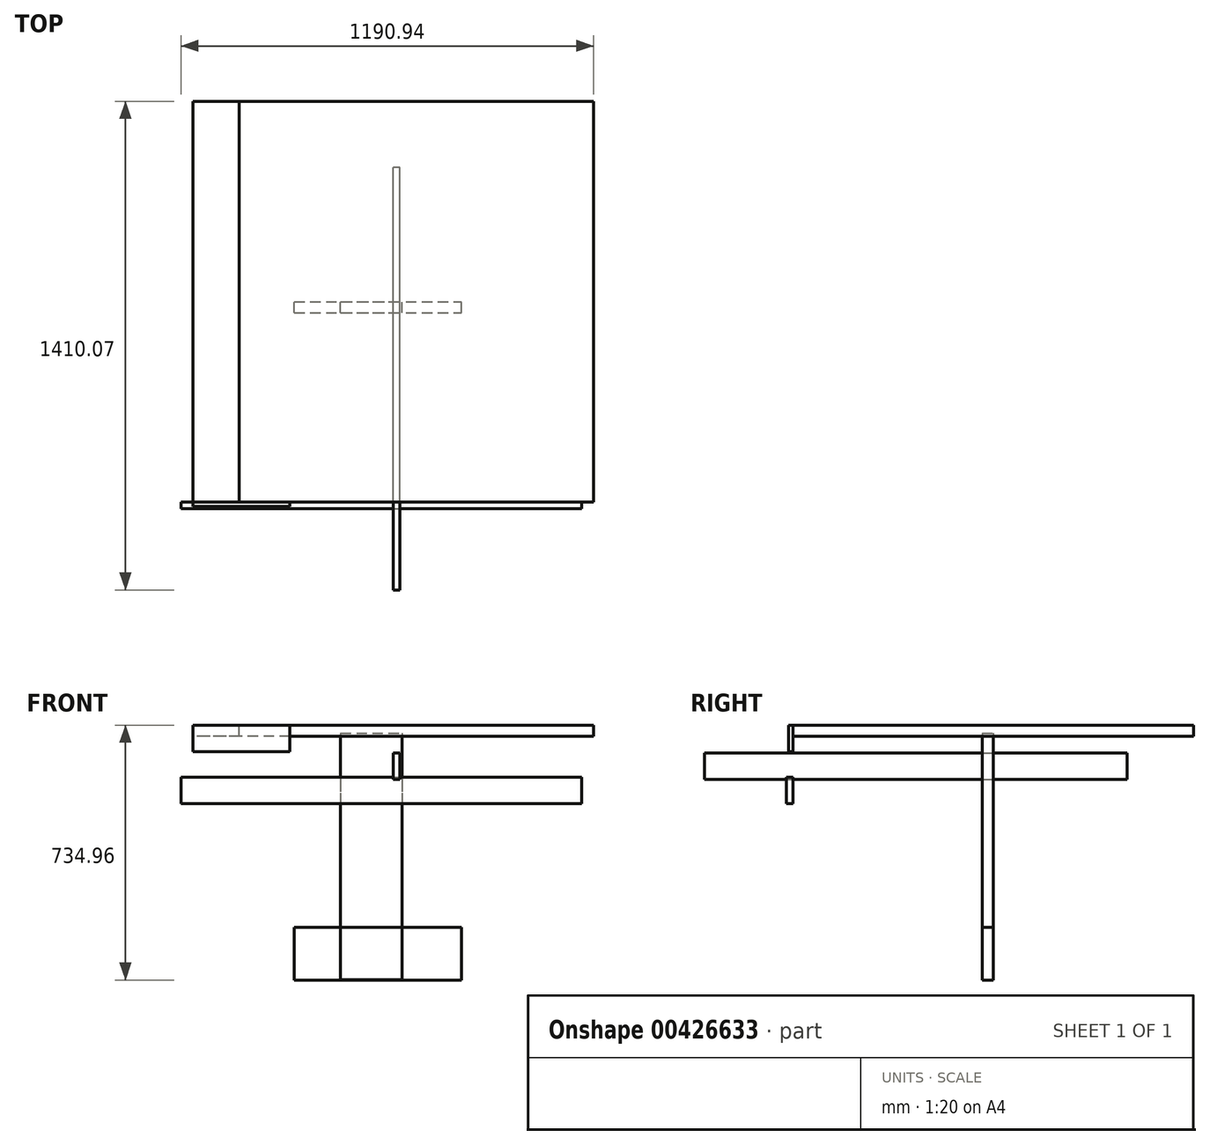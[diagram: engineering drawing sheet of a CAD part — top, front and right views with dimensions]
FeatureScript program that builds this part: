
annotation { "Feature Type Name" : "Feature", "Feature Type Description" : "" }
export const myFeature = defineFeature(function(context is Context, id is Id, definition is map)
    precondition{}
    {
        {
            var Q0;
            Q0=qCreatedBy(makeId("Top.planeOp"),FACE);
            var sketch = newSketch(context, id + "F0", { "sketchPlane" : qUnion([Q0])});
            skLineSegment(sketch, "E0.bottom", {"start": v(577.85, 577.85) * mm, "end": v(-577.85, 577.85) * mm});
            skLineSegment(sketch, "E0.top", {"start": v(577.85, -577.85) * mm, "end": v(-577.85, -577.85) * mm});
            skLineSegment(sketch, "E0.left", {"start": v(577.85, 577.85) * mm, "end": v(577.85, -577.85) * mm});
            skLineSegment(sketch, "E0.right", {"start": v(-577.85, 577.85) * mm, "end": v(-577.85, -577.85) * mm});
            skPoint(sketch, "E0.middle", {"position": v(0, 0) * mm});
            skLineSegment(sketch, "E1", {"start": v(0, 0) * mm, "end": v(0, 577.85) * mm, "construction": true});
            skLineSegment(sketch, "E2", {"start": v(0, 0) * mm, "end": v(0, -577.85) * mm, "construction": true});
            skLineSegment(sketch, "E3", {"start": v(0, -577.85) * mm, "end": v(0, 0) * mm, "construction": true});
            skLineSegment(sketch, "E4", {"start": v(0, 0) * mm, "end": v(577.85, 0) * mm, "construction": true});
            skLineSegment(sketch, "E5", {"start": v(577.85, 0) * mm, "end": v(-577.85, 0) * mm, "construction": true});
            skSolve(sketch);
        }
        {
            var Q0;
            Q0 = qSketchRegion(id + "F0", true);
            extrude(context, id + "F1", {"entities" : qUnion([Q0]), "depth" : 31.75 * mm});
        }
        {
            var Q0;
            Q0=makeQuery(id+"F1.opExtrude","SWEPT_FACE",FACE,{"disambiguationData":[OSD([sQuery(id+"F0.wireOp",EDGE,"E0.top")])]});
            var sketch = newSketch(context, id + "F2", { "sketchPlane" : qUnion([Q0])});
            skLineSegment(sketch, "E6.bottom", {"start": v(577.85, 31.75) * mm, "end": v(369.14, 31.75) * mm});
            skLineSegment(sketch, "E6.top", {"start": v(577.85, 0) * mm, "end": v(369.14, 0) * mm});
            skLineSegment(sketch, "E6.left", {"start": v(577.85, 31.75) * mm, "end": v(577.85, 0) * mm});
            skLineSegment(sketch, "E6.right", {"start": v(369.14, 31.75) * mm, "end": v(369.14, 0) * mm});
            skLineSegment(sketch, "E7.bottom", {"start": v(-613.1, -117.95) * mm, "end": v(542.6, -117.95) * mm});
            skLineSegment(sketch, "E7.top", {"start": v(-613.1, -194.15) * mm, "end": v(542.6, -194.15) * mm});
            skLineSegment(sketch, "E7.left", {"start": v(-613.1, -117.95) * mm, "end": v(-613.1, -194.15) * mm});
            skLineSegment(sketch, "E7.right", {"start": v(542.6, -117.95) * mm, "end": v(542.6, -194.15) * mm});
            skSolve(sketch);
        }
        {
            var Q0;
            Q0=makeQuery(id+"F1.opExtrude","SWEPT_FACE",FACE,{"disambiguationData":[OSD([sQuery(id+"F0.wireOp",EDGE,"E0.top")])]});
            var sketch = newSketch(context, id + "F3", { "sketchPlane" : qUnion([Q0])});
            skLineSegment(sketch, "E8.bottom", {"start": v(-577.85, 31.75) * mm, "end": v(-298.45, 31.75) * mm});
            skLineSegment(sketch, "E8.top", {"start": v(-577.85, -44.45) * mm, "end": v(-298.45, -44.45) * mm});
            skLineSegment(sketch, "E8.left", {"start": v(-577.85, 31.75) * mm, "end": v(-577.85, -44.45) * mm});
            skLineSegment(sketch, "E8.right", {"start": v(-298.45, 31.75) * mm, "end": v(-298.45, -44.45) * mm});
            skSolve(sketch);
        }
        {
            var Q0;
            Q0=qCreatedBy(makeId("Front.planeOp"),FACE);
            var sketch = newSketch(context, id + "F4", { "sketchPlane" : qUnion([Q0])});
            skLineSegment(sketch, "E9.bottom", {"start": v(-152.48, 8.4) * mm, "end": v(25.32, 8.4) * mm});
            skLineSegment(sketch, "E9.top", {"start": v(-152.48, -702.8) * mm, "end": v(25.32, -702.8) * mm});
            skLineSegment(sketch, "E9.left", {"start": v(-152.48, 8.4) * mm, "end": v(-152.48, -702.8) * mm});
            skLineSegment(sketch, "E9.right", {"start": v(25.32, 8.4) * mm, "end": v(25.32, -702.8) * mm});
            skSolve(sketch);
        }
        {
            var Q0;
            Q0=makeQuery(id+"F4.imprint","IMPRINT",FACE,{"disambiguationData":[TD([[makeQuery(id+"F4.imprint","IMPRINT",EDGE,{"derivedFrom":sQuery(id+"F4.wireOp",EDGE,"E9.bottom")}),-1.0]])]});
            extrude(context, id + "F5", {"entities" : qUnion([Q0]), "depth" : 31.75 * mm});
        }
        {
            var Q0;
            Q0=makeQuery(id+"F1.opExtrude","CAP_FACE",FACE,{"disambiguationData":[OSD([sQuery(id+"F0.wireOp",EDGE,"E0.bottom"),sQuery(id+"F0.wireOp",EDGE,"E0.top"),sQuery(id+"F0.wireOp",EDGE,"E0.left"),sQuery(id+"F0.wireOp",EDGE,"E0.right")])],"isStart":false});
            var sketch = newSketch(context, id + "F6", { "sketchPlane" : qUnion([Q0])});
            skLineSegment(sketch, "E10.bottom", {"start": v(-577.85, 577.85) * mm, "end": v(-444.5, 577.85) * mm});
            skLineSegment(sketch, "E10.top", {"start": v(-577.85, -577.85) * mm, "end": v(-444.5, -577.85) * mm});
            skLineSegment(sketch, "E10.left", {"start": v(-577.85, 577.85) * mm, "end": v(-577.85, -577.85) * mm});
            skLineSegment(sketch, "E10.right", {"start": v(-444.5, 577.85) * mm, "end": v(-444.5, -577.85) * mm});
            skSolve(sketch);
        }
        {
            var Q0;
            Q0=makeQuery(id+"F6.imprint","IMPRINT",FACE,{"disambiguationData":[TD([[makeQuery(id+"F6.imprint","IMPRINT",EDGE,{"derivedFrom":sQuery(id+"F6.wireOp",EDGE,"E10.bottom")}),1.0]])]});
            extrude(context, id + "F7", {"entities" : qUnion([Q0]), "oppositeDirection" : true, "depth" : 31.75 * mm});
        }
        {
            var Q0;
            Q0 = qSketchRegion(id + "F3", true);
            extrude(context, id + "F8", {"entities" : qUnion([Q0]), "depth" : 12.7 * mm});
        }
        {
            var Q0;
            Q0 = qSketchRegion(id + "F2", true);
            var Q1;
            Q1=makeQuery(id+"F2.imprint","IMPRINT",FACE,{"disambiguationData":[TD([[makeQuery(id+"F2.imprint","IMPRINT",EDGE,{"derivedFrom":sQuery(id+"F2.wireOp",EDGE,"E7.bottom")}),-1.0]])]});
            extrude(context, id + "F9", {"entities" : qUnion([Q0, Q1]), "depth" : 19.05 * mm});
        }
        {
            var Q0;
            Q0=makeQuery(id+"F9.opExtrude","SWEPT_BODY",BODY,{"disambiguationData":[OSD([sQuery(id+"F2.wireOp",EDGE,"E6.bottom"),sQuery(id+"F2.wireOp",EDGE,"E6.top"),sQuery(id+"F2.wireOp",EDGE,"E6.left"),sQuery(id+"F2.wireOp",EDGE,"E6.right")])]});
            deleteBodies(context, id + "F10", {"entities" : qUnion([Q0])});
        }
        {
            var Q0;
            Q0=qCreatedBy(makeId("Right.planeOp"),FACE);
            var sketch = newSketch(context, id + "F11", { "sketchPlane" : qUnion([Q0])});
            skLineSegment(sketch, "E11.bottom", {"start": v(358.73, 101.84) * mm, "end": v(150.01, 101.84) * mm});
            skLineSegment(sketch, "E11.top", {"start": v(358.73, 70.09) * mm, "end": v(150.01, 70.09) * mm});
            skLineSegment(sketch, "E11.left", {"start": v(358.73, 101.84) * mm, "end": v(358.73, 70.09) * mm});
            skLineSegment(sketch, "E11.right", {"start": v(150.01, 101.84) * mm, "end": v(150.01, 70.09) * mm});
            skLineSegment(sketch, "E12.bottom", {"start": v(-832.22, -47.86) * mm, "end": v(386.98, -47.86) * mm});
            skLineSegment(sketch, "E12.top", {"start": v(-832.22, -124.06) * mm, "end": v(386.98, -124.06) * mm});
            skLineSegment(sketch, "E12.left", {"start": v(-832.22, -47.86) * mm, "end": v(-832.22, -124.06) * mm});
            skLineSegment(sketch, "E12.right", {"start": v(386.98, -47.86) * mm, "end": v(386.98, -124.06) * mm});
            skSolve(sketch);
        }
        {
            var Q0;
            Q0=makeQuery(id+"F11.imprint","IMPRINT",FACE,{"disambiguationData":[TD([[makeQuery(id+"F11.imprint","IMPRINT",EDGE,{"derivedFrom":sQuery(id+"F11.wireOp",EDGE,"E12.bottom")}),-1.0]])]});
            extrude(context, id + "F12", {"entities" : qUnion([Q0]), "depth" : 19.05 * mm});
        }
        {
            var Q0;
            Q0=qCreatedBy(makeId("Front.planeOp"),FACE);
            var sketch = newSketch(context, id + "F13", { "sketchPlane" : qUnion([Q0])});
            skLineSegment(sketch, "E13.bottom", {"start": v(-286.05, -550.81) * mm, "end": v(196.55, -550.81) * mm});
            skLineSegment(sketch, "E13.top", {"start": v(-286.05, -703.21) * mm, "end": v(196.55, -703.21) * mm});
            skLineSegment(sketch, "E13.left", {"start": v(-286.05, -550.81) * mm, "end": v(-286.05, -703.21) * mm});
            skLineSegment(sketch, "E13.right", {"start": v(196.55, -550.81) * mm, "end": v(196.55, -703.21) * mm});
            skSolve(sketch);
        }
        {
            var Q0;
            Q0 = qSketchRegion(id + "F13", true);
            extrude(context, id + "F14", {"entities" : qUnion([Q0]), "depth" : 31.75 * mm, "offsetDistance" : 25.4 * mm});
        }
    });
